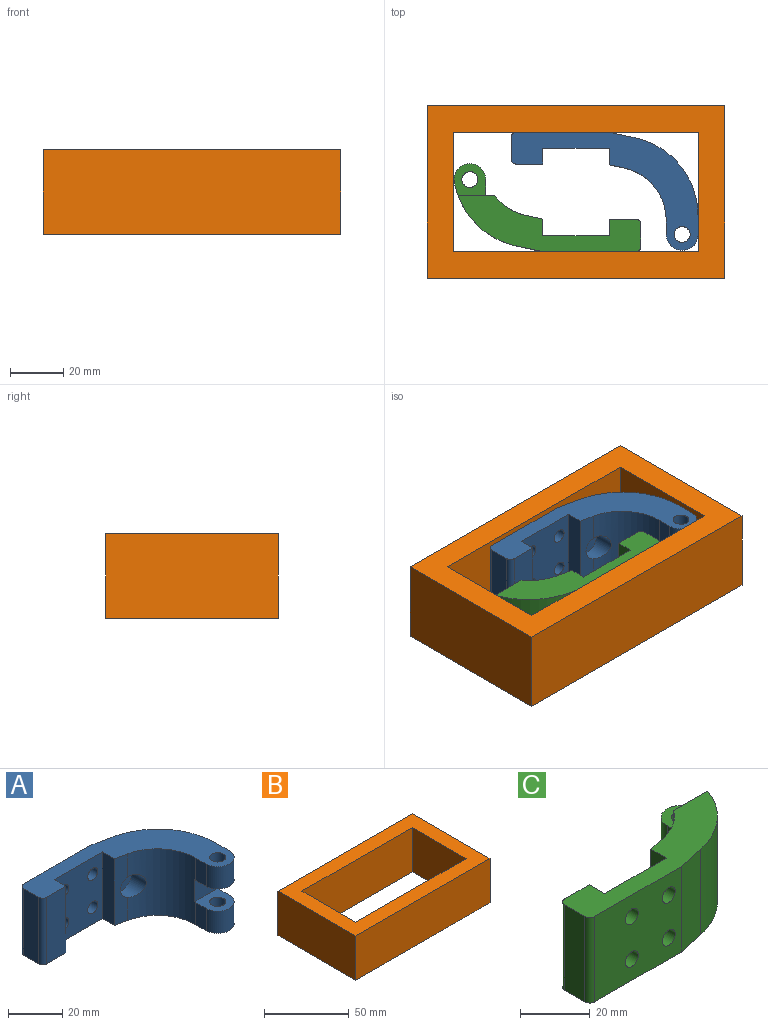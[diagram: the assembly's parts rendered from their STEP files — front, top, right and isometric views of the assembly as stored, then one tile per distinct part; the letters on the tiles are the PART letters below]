
ASSEMBLY  parts=3 mates=6
PART A: 30 faces, bbox 71.9x45.9x31.4 mm
  f0: cylinder r=20mm len=30mm, axis (0,0,1), area 749.2mm2, adj f1,f5,f16,f18,f19,f21,f22,f23
  f1: plane 10x5.46mm, normal (-1,0,0), area 54.6mm2, adj f0,f3,f19,f23
  f2: cylinder r=3mm len=10mm, axis (0,0,-1), area 188.5mm2, adj f19,f23
  f3: cylinder r=6mm len=12mm, axis (0,0,-1), area 188.5mm2, adj f1,f4,f19,f23
  f4: plane 30x7.08mm, normal (1,0,0), area 152.3mm2, adj f3,f6,f18,f19,f20,f21,f22,f23
  f5: plane 10x5.46mm, normal (-1,0,0), area 54.6mm2, adj f0,f6,f18,f22
  f6: cylinder r=6mm len=12mm, axis (0,0,-1), area 188.5mm2, adj f4,f5,f18,f22
  f7: plane 30x9.77mm, normal (0.21,0.98,0), area 299.6mm2, adj f8,f18,f19,f20
  f8: plane 35x30mm, normal (0,1,0), area 963.4mm2, adj f7,f9,f18,f19,f24,f25,f26,f27
  f9: cylinder r=2mm len=30mm, axis (0,0,-1), area 94.2mm2, adj f8,f10,f18,f19
  f10: plane 30x8mm, normal (-1,0,0), area 240mm2, adj f9,f11,f18,f19
  f11: cylinder r=2mm len=30mm, axis (0,0,-1), area 94.2mm2, adj f10,f12,f18,f19
  f12: plane 30x10mm, normal (0,-1,0), area 300mm2, adj f11,f13,f18,f19
  f13: plane 30x6mm, normal (1,0,0), area 180mm2, adj f12,f14,f18,f19
  f14: plane 30x25mm, normal (0,-1,0), area 663.4mm2, adj f13,f15,f18,f19,f24,f25,f26,f27
  f15: plane 30x6.27mm, normal (-1,0,0), area 188.1mm2, adj f14,f16,f18,f19
  f16: plane 31.36x7.04mm, normal (-0.21,-0.98,0), area 152.2mm2, adj f0,f15,f18,f19,f28
  f17: cylinder r=3mm len=10mm, axis (0,0,-1), area 188.5mm2, adj f18,f22
  f18: plane 70.5x44.5mm, normal (0,0,1), area 911.5mm2, adj f0,f4,f5,f6,f7,f8,f9,f10
  f19: plane 70.5x44.5mm, normal (0,0,-1), area 911.5mm2, adj f0,f1,f2,f3,f4,f7,f8,f9
  f20: cylinder r=30mm len=30mm, axis (0,0,1), area 1224.3mm2, adj f4,f7,f18,f19
  f21: plane 12.02x10.01mm, normal (0,-1,0), area 120mm2, adj f0,f4,f22,f23
  f22: plane 12.02x12.01mm, normal (0,0,-1), area 100.3mm2, adj f0,f4,f5,f6,f17,f21
  f23: plane 12.02x12.01mm, normal (0,0,1), area 100.3mm2, adj f0,f1,f2,f3,f4,f21
  f24: cylinder r=2.62mm len=6mm, axis (0,-1,0), area 99mm2, adj f8,f14
  f25: cylinder r=2.62mm len=6mm, axis (0,-1,0), area 99mm2, adj f8,f14
  f26: cylinder r=2.62mm len=6mm, axis (0,-1,0), area 99mm2, adj f8,f14
  f27: cylinder r=2.62mm len=6mm, axis (0,-1,0), area 99mm2, adj f8,f14
  f28: cylinder r=5mm len=10mm, axis (0,1,0), area 186.8mm2, adj f0,f16,f29
  f29: plane 10x10mm, normal (0,-1,0), area 78.5mm2, adj f28
PART B: 10 faces, bbox 112x65x32 mm
  f0: plane 65x32mm, normal (1,0,0), area 2080mm2, adj f1,f7,f8,f9
  f1: plane 112x32mm, normal (0,1,0), area 3584mm2, adj f0,f2,f8,f9
  f2: plane 65x32mm, normal (-1,0,0), area 2080mm2, adj f1,f7,f8,f9
  f3: plane 92x32mm, normal (0,-1,0), area 2944mm2, adj f4,f6,f8,f9
  f4: plane 45x32mm, normal (-1,0,0), area 1440mm2, adj f3,f5,f8,f9
  f5: plane 92x32mm, normal (0,1,0), area 2944mm2, adj f4,f6,f8,f9
  f6: plane 45x32mm, normal (1,0,0), area 1440mm2, adj f3,f5,f8,f9
  f7: plane 112x32mm, normal (0,-1,0), area 3584mm2, adj f0,f2,f8,f9
  f8: plane 112x65mm, normal (0,0,1), area 3140mm2, adj f0,f1,f2,f3,f4,f5,f6,f7
  f9: plane 112x65mm, normal (0,0,-1), area 3140mm2, adj f0,f1,f2,f3,f4,f5,f6,f7
PART C: 26 faces, bbox 70.5x33.2x30 mm
  f0: cylinder r=20mm len=30mm, axis (0,0,-1), area 374.9mm2, adj f2,f3,f4,f16,f23
  f1: cylinder r=6mm len=12mm, axis (0,0,-1), area 188.5mm2, adj f14,f15,f17,f25
  f2: plane 68.98x21.16mm, normal (0,0,1), area 670.5mm2, adj f0,f4,f5,f6,f7,f8,f9,f10
  f3: plane 68.98x21.16mm, normal (0,0,-1), area 670.5mm2, adj f0,f4,f5,f6,f7,f8,f9,f10
  f4: plane 30x6.39mm, normal (-0.21,0.98,0), area 167.1mm2, adj f0,f2,f3,f5,f23
  f5: plane 30x6.27mm, normal (-1,0,0), area 188.1mm2, adj f2,f3,f4,f6
  f6: plane 30x25mm, normal (0,1,0), area 663.4mm2, adj f2,f3,f5,f7,f19,f20,f21,f22
  f7: plane 30x6.27mm, normal (1,0,0), area 188.1mm2, adj f2,f3,f6,f8
  f8: plane 30x10mm, normal (0,1,0), area 300mm2, adj f2,f3,f7,f9
  f9: cylinder r=2mm len=30mm, axis (0,0,-1), area 94.2mm2, adj f2,f3,f8,f10
  f10: plane 30x8.27mm, normal (-1,0,0), area 248.1mm2, adj f2,f3,f9,f11
  f11: cylinder r=2mm len=30mm, axis (0,0,-1), area 94.2mm2, adj f2,f3,f10,f12
  f12: plane 35x30mm, normal (0,-1,0), area 963.4mm2, adj f2,f3,f11,f13,f19,f20,f21,f22
  f13: plane 30x10.08mm, normal (0.21,-0.98,0), area 309.3mm2, adj f2,f3,f12,f14
  f14: cylinder r=30mm len=30mm, axis (0,0,-1), area 969.8mm2, adj f1,f2,f3,f13,f15,f16,f17
  f15: plane 12x12mm, normal (0,0,1), area 96.4mm2, adj f1,f14,f16,f18,f25
  f16: plane 30x13.8mm, normal (0,1,0), area 309.1mm2, adj f0,f2,f3,f14,f15,f17,f25
  f17: plane 12x12mm, normal (0,0,-1), area 96.4mm2, adj f1,f14,f16,f18,f25
  f18: cylinder r=3mm len=10mm, axis (0,0,-1), area 188.5mm2, adj f15,f17
  f19: cylinder r=2.62mm len=6mm, axis (0,1,0), area 99mm2, adj f6,f12
  f20: cylinder r=2.62mm len=6mm, axis (0,1,0), area 99mm2, adj f6,f12
  f21: cylinder r=2.62mm len=6mm, axis (0,1,0), area 99mm2, adj f6,f12
  f22: cylinder r=2.62mm len=6mm, axis (0,1,0), area 99mm2, adj f6,f12
  f23: cylinder r=5mm len=10mm, axis (0,1,0), area 220.5mm2, adj f0,f4,f24
  f24: plane 10x10mm, normal (0,1,0), area 78.5mm2, adj f23
  f25: plane 10x6mm, normal (-1,0,0), area 60mm2, adj f1,f15,f16,f17
PLACE A t=(0.18,-3.67,9.41)mm fixed
PLACE B t=(0.18,12.33,-5.59)mm
PLACE C rot(axis=(0,1,0),180deg) t=(0.18,16.99,9.41)mm
MATE cylindrical C.f19 <-> A.f26  axis (0,1,0) through (7.68,-7.17,16.91)mm
MATE planar A.f19 <-> B.f9  axis (0,0,-1) through (17.56,33.79,-5.59)mm
MATE planar C.f12 <-> B.f5  axis (0,-1,0) through (5.63,-10.17,9.41)mm
MATE planar A.f8 <-> B.f3  axis (0,1,0) through (-5.27,34.83,9.41)mm
MATE planar C.f2 <-> A.f19  axis (0,0,-1) through (-17.37,-9.09,-5.59)mm
MATE cylindrical A.f24 <-> C.f21  axis (0,-1,0) through (-7.32,28.83,1.91)mm
